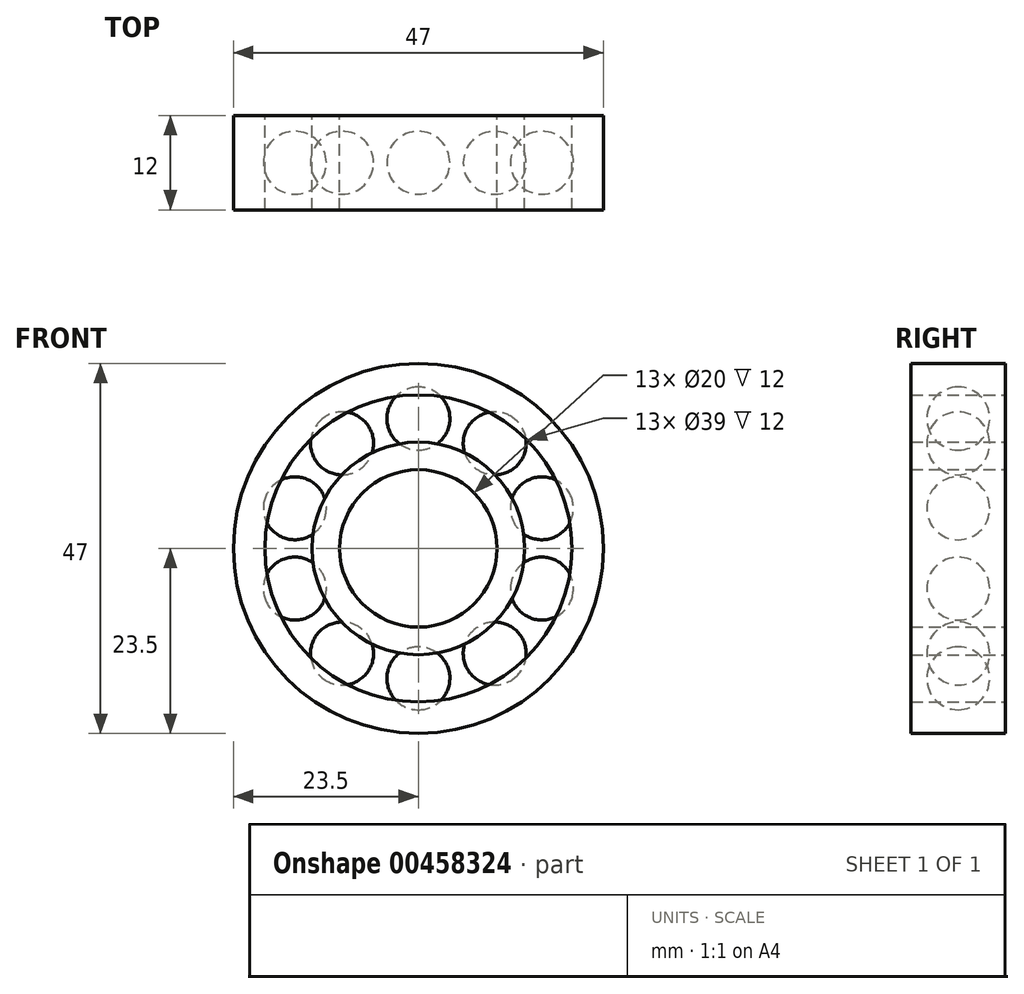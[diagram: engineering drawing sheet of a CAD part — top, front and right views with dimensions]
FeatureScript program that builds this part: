
annotation { "Feature Type Name" : "Feature", "Feature Type Description" : "" }
export const myFeature = defineFeature(function(context is Context, id is Id, definition is map)
    precondition{}
    {
        {
            var Q0;
            Q0=qCreatedBy(makeId("Front.planeOp"),FACE);
            var sketch = newSketch(context, id + "F0", { "sketchPlane" : qUnion([Q0])});
            skCircle(sketch, "E0", {"center": v(0, 0) * mm, "radius": 10 * mm});
            skCircle(sketch, "E1", {"center": v(0, 0) * mm, "radius": 13.5 * mm});
            skSolve(sketch);
        }
        {
            var Q0;
            Q0=makeQuery(id+"F0.imprint","IMPRINT",FACE,{"disambiguationData":[TD([[makeQuery(id+"F0.imprint","IMPRINT",EDGE,{"derivedFrom":sQuery(id+"F0.wireOp",EDGE,"E0")}),-1.0]])]});
            extrude(context, id + "F1", {"entities" : qUnion([Q0]), "depth" : 12 * mm});
        }
        {
            var Q0;
            Q0=qCreatedBy(makeId("Front.planeOp"),FACE);
            var sketch = newSketch(context, id + "F2", { "sketchPlane" : qUnion([Q0])});
            skCircle(sketch, "E2", {"center": v(0, 0) * mm, "radius": 19.5 * mm});
            skCircle(sketch, "E3", {"center": v(0, 0) * mm, "radius": 23.5 * mm});
            skSolve(sketch);
        }
        {
            var Q0;
            Q0=makeQuery(id+"F2.imprint","IMPRINT",FACE,{"disambiguationData":[TD([[makeQuery(id+"F2.imprint","IMPRINT",EDGE,{"derivedFrom":sQuery(id+"F2.wireOp",EDGE,"E2")}),-1.0]])]});
            extrude(context, id + "F3", {"entities" : qUnion([Q0]), "depth" : 12 * mm});
        }
        {
            var Q0;
            Q0=qCreatedBy(makeId("Front.planeOp"),FACE);
            cPlane(context, id + "F4", {"entities" : qUnion([Q0]), "cplaneType" : CPlaneType.OFFSET, "offset" : 6 * mm, "width" : 150 * mm, "height" : 150 * mm});
        }
        {
            var Q0;
            Q0=qCreatedBy(id+"F4.planeOp",FACE);
            var sketch = newSketch(context, id + "F5", { "sketchPlane" : qUnion([Q0])});
            skArc(sketch, "E4", {"start": v(0, 12.5) * mm, "mid": v(4, 16.5) * mm, "end": v(0, 20.5) * mm});
            skLineSegment(sketch, "E5", {"start": v(0, 20.5) * mm, "end": v(0, 12.5) * mm});
            skPoint(sketch, "E6.orphan", {"position": v(0, 38.36) * mm});
            skSolve(sketch);
        }
        {
            var Q0;
            Q0 = qSketchRegion(id + "F5", true);
            var Q1;
            Q1=sQuery(id+"F5.wireOp",EDGE,"E5");
            revolve(context, id + "F6", {"entities" : qUnion([Q0]), "axis" : qUnion([Q1]), "revolveType" : RevolveType.FULL});
        }
        {
            var Q0;
            Q0=qCreatedBy(makeId("Right.planeOp"),FACE);
            var sketch = newSketch(context, id + "F7", { "sketchPlane" : qUnion([Q0])});
            skLineSegment(sketch, "E7", {"start": v(0, 0) * mm, "end": v(-19.57, 0) * mm, "construction": true});
            skSolve(sketch);
        }
        {
            var Q0;
            Q0=makeQuery(id+"F6.opRevolve","SWEPT_BODY",BODY,{"disambiguationData":[OSD([sQuery(id+"F5.wireOp",EDGE,"E4"),sQuery(id+"F5.wireOp",EDGE,"E5")])]});
            var Q1;
            Q1=sQuery(id+"F7.wireOp",EDGE,"E7");
            circularPattern(context, id + "F8", {"entities" : qUnion([Q0]), "axis" : qUnion([Q1]), "angle" : 360 * degree, "instanceCount" : 10, "equalSpace" : true});
        }
    });
